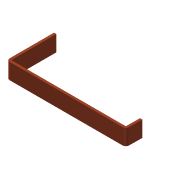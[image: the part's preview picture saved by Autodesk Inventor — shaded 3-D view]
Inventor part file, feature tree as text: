
AUTODESK INVENTOR PART (.ipt)
format: ipt  version: 2016 SP2 (Build 200236200, 236)  size: 102,912 bytes
history: native  units: mm
features: fillet x2, extrude x1
ambient origin geometry x8: Origin, YZ Plane, XZ Plane, XY Plane, X Axis, Y Axis, Z Axis, Center Point
bodies: Body1 (feature_tree)
feature tree (3):
  extrude  "Extrusion3"  Depth=41.599591mm
  fillet  "Fillet1"  Radius=301.0mm
  fillet  "Fillet2"  Radius=115.0mm
